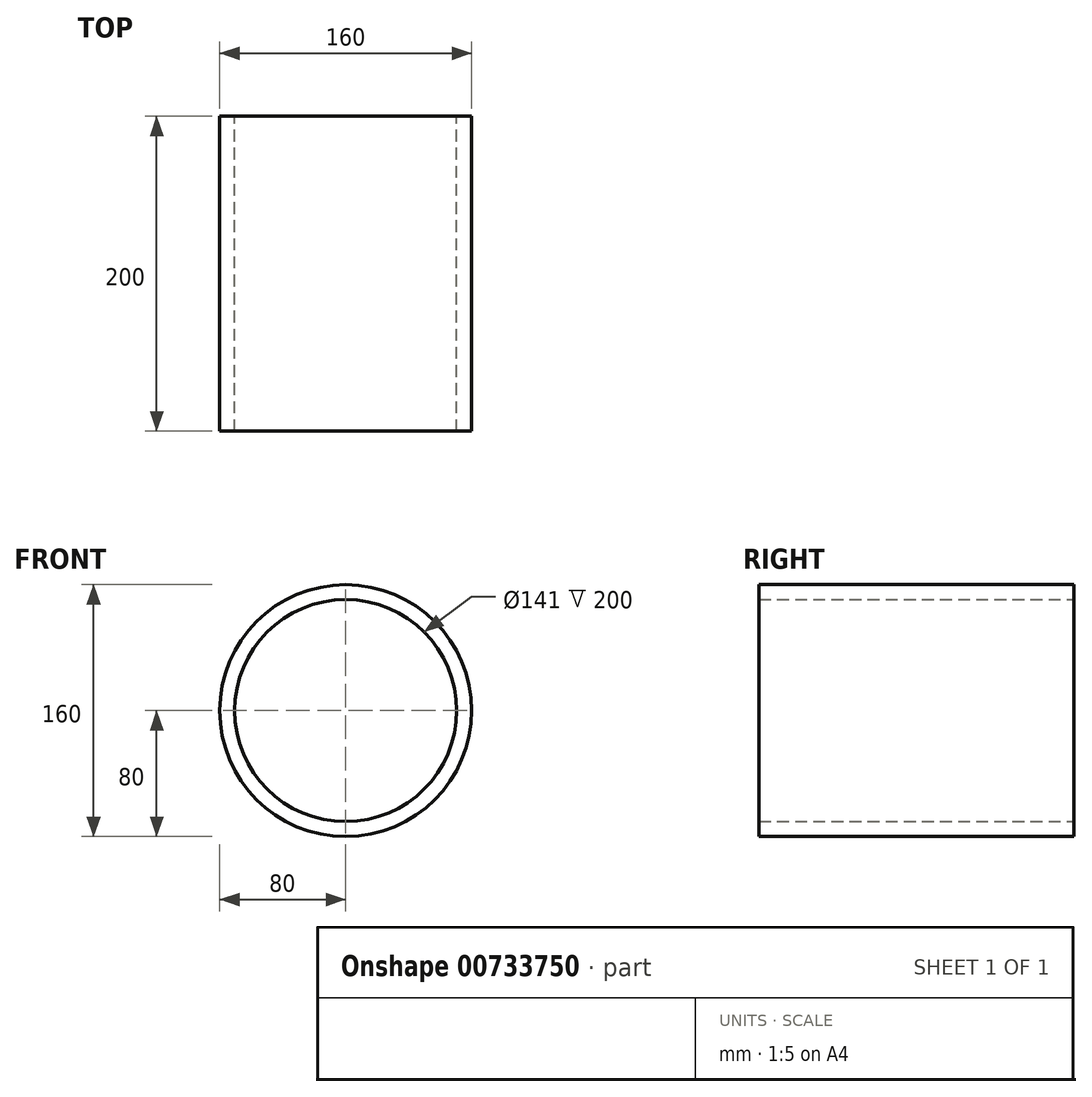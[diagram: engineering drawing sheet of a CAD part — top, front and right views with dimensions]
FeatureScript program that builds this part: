
annotation { "Feature Type Name" : "Feature", "Feature Type Description" : "" }
export const myFeature = defineFeature(function(context is Context, id is Id, definition is map)
    precondition{}
    {
        {
            var Q0;
            Q0=qCreatedBy(makeId("Front.planeOp"),FACE);
            var sketch = newSketch(context, id + "F0", { "sketchPlane" : qUnion([Q0])});
            skCircle(sketch, "E0", {"center": v(0, 0) * mm, "radius": 80 * mm});
            skCircle(sketch, "E1", {"center": v(0, 0) * mm, "radius": 70.5 * mm});
            skSolve(sketch);
        }
        {
            var Q0;
            Q0=qSketchRegion(id+"F0",true);
            extrude(context, id + "F1", {"entities" : qUnion([Q0]), "depth" : 200 * mm, "offsetDistance" : 25 * mm});
        }
    });
